# Revit family: IS_IdealSystem_W3705_BIM_NL
name_source: partatom
category: Plumbing Fixtures
revit_build: Autodesk Revit MEP 2014 (Build: 20130308_1515(x64)
units: mm (PartAtom-declared; Revit-internal decimal feet)

## types (1)
- W370567 - INBOUWRESERVOIR ZONDER AFDEKPLAAT IS
    Accessories = www.idealstandardnederland.nl
    AreaUnits = millimeters
    Assembly Code = C1030200
    AssetType = Vast
    BIMObjectName = ISI_IdealStandard_WcCisterns_W370567
    BREEAMApproved = No
    BarCode = 3800828021747
    Brand = Ideal Standard
    CWFU = 0
    ConnectionType = Sanitair
    Cost = 0 $
    Default Elevation = 0 mm  [stored 0 ft]
    Description = Inbouwspoelreservoir. 3/6 liter spoeling. Exclusief drukplaat.
    DurationUnit = jaar
    ECA = No
    ExpectedLife = 25
    Features = Inbouwspoelreservoir. 3/6 liter spoeling. Exclusief drukplaat.
    HWFU = 0
    IfcExportAs = IfcSanitaryTerminalType
    IfcExportType = Inbouwspoelreservoir
    InstallationInstructions = http://www.idealstandardnederland.nl
    LinearUnits = millimeters
    ManufacturerURL = www.idealstandardnederland.nl
    Model = W370567
    ModelNumber = W370567
    ModelReference = Inbouwspoelreservoir. 3/6 liter spoeling. Exclusief drukplaat.
    NBSDescription = WC cisterns
    NBSReference = 45-35-70/383
    Name = WcCisterns_W370567_IdealStandard
    NettWeight = 10.65 kg
    NominalDepth = 333 mm
    NominalLength = 0 mm  [stored 0 ft]
    NominalWidth = 350 mm  [stored 1.14829 ft]
    ProductInformation = http://www.idealstandardnederland.nl
    Shape = Gesculptuurd
    Size = 350 x 262 x 1100 mm
    Space = Internal
    SpilloverLevel = 0 mm  [stored 0 ft]
    URL = www.idealstandardnederland.nl
    Uniclass2015Code = Pr_40_20_93_89
    Uniclass2015Title = WC cisterns
    Uniclass2015Version = Products v1.1
    Version = 1
    VolumeUnits = liter
    WFU = 0
    WRAS = No
    WarrantyDescription = Fabrieksgarantie
    WarrantyDurationParts = 5
    WarrantyDurationUnit = jaar
    WaterEfficientProduct = No

note: [stored X ft] marks values corroborated as IEEE doubles in the binary element streams (Revit-internal decimal feet)

## geometry (parser evidence)
native form markers: Blend x4, Sweep x7
no freeform markers — native parametric forms only
